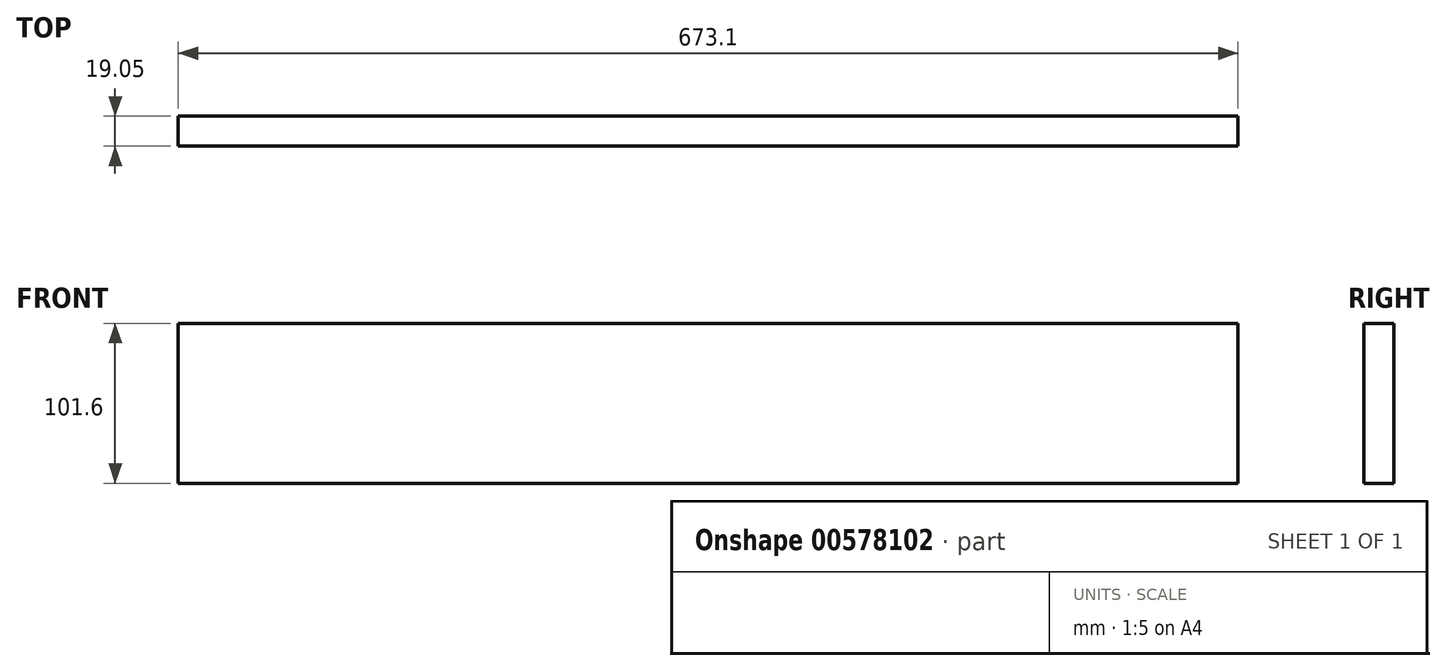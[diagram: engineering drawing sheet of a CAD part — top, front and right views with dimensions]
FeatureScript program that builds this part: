
annotation { "Feature Type Name" : "Feature", "Feature Type Description" : "" }
export const myFeature = defineFeature(function(context is Context, id is Id, definition is map)
    precondition{}
    {
        {
            var Q0;
            Q0=qCreatedBy(makeId("Front.planeOp"),FACE);
            var sketch = newSketch(context, id + "F0", { "sketchPlane" : qUnion([Q0])});
            skLineSegment(sketch, "E0.bottom", {"start": v(0, 0) * mm, "end": v(673.1, 0) * mm});
            skLineSegment(sketch, "E0.top", {"start": v(0, 101.6) * mm, "end": v(673.1, 101.6) * mm});
            skLineSegment(sketch, "E0.left", {"start": v(0, 0) * mm, "end": v(0, 101.6) * mm});
            skLineSegment(sketch, "E0.right", {"start": v(673.1, 0) * mm, "end": v(673.1, 101.6) * mm});
            skSolve(sketch);
        }
        {
            var Q0;
            Q0 = qSketchRegion(id + "F0", true);
            extrude(context, id + "F1", {"entities" : qUnion([Q0]), "depth" : 19.05 * mm, "offsetDistance" : 25.4 * mm});
        }
    });
